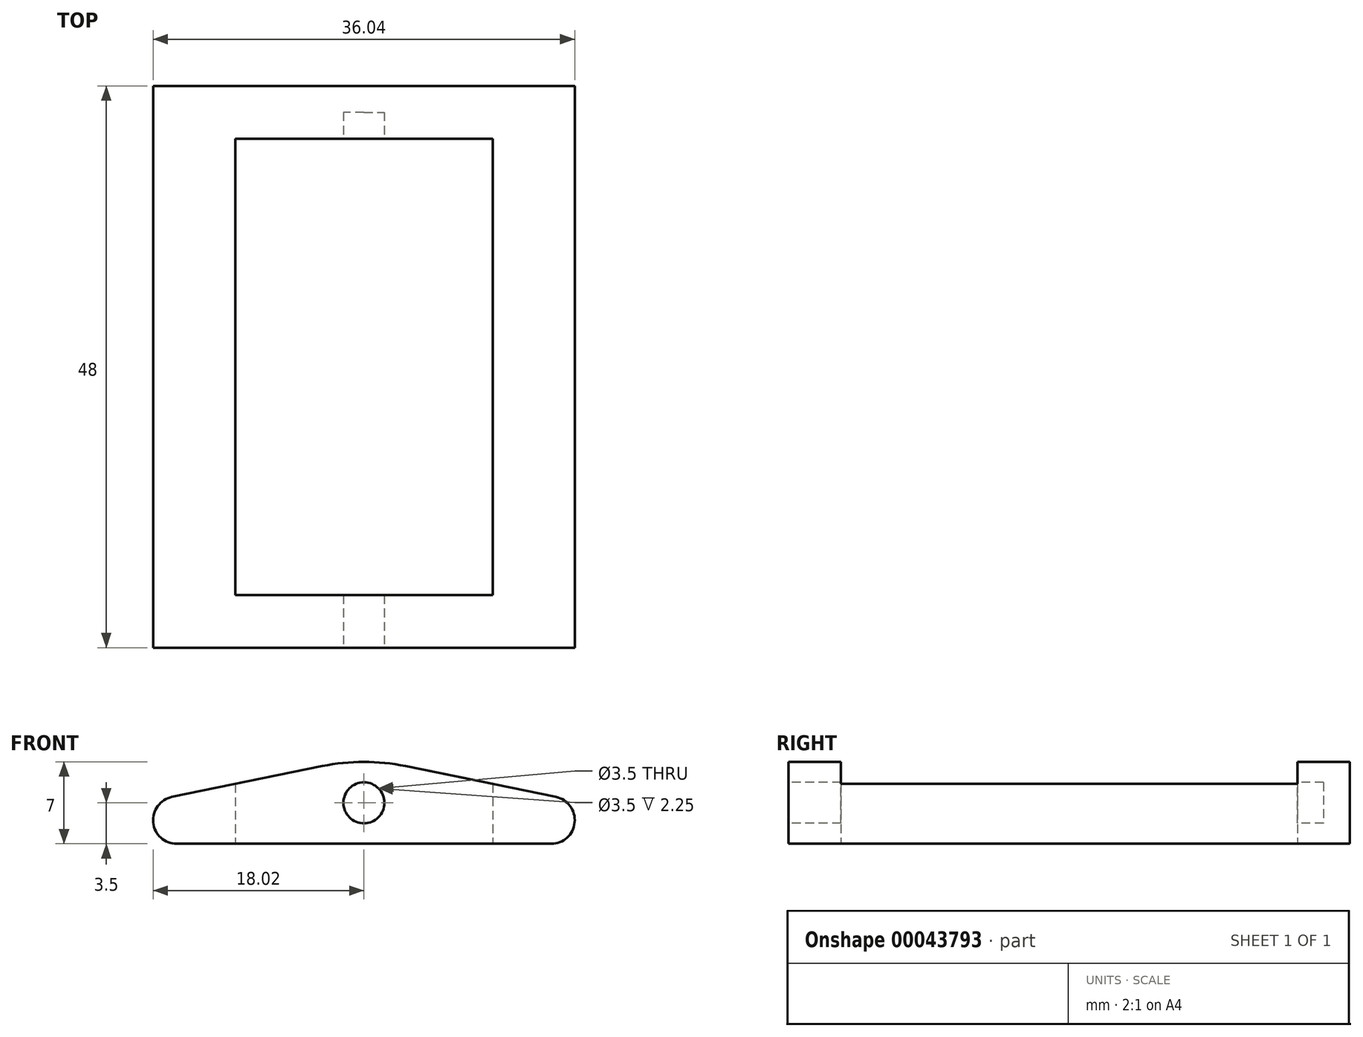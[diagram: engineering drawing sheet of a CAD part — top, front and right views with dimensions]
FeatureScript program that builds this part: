
annotation { "Feature Type Name" : "Feature", "Feature Type Description" : "" }
export const myFeature = defineFeature(function(context is Context, id is Id, definition is map)
    precondition{}
    {
        {
            var Q0;
            Q0=qCreatedBy(makeId("Front.planeOp"),FACE);
            var sketch = newSketch(context, id + "F0", { "sketchPlane" : qUnion([Q0])});
            skLineSegment(sketch, "E0", {"start": v(-16, 0) * mm, "end": v(16, 0) * mm});
            skArc(sketch, "E1", {"start": v(16, 0) * mm, "mid": v(18.01, 1.82) * mm, "end": v(16.4, 4) * mm});
            skArc(sketch, "E2", {"start": v(3.55, 6.64) * mm, "mid": v(0, 7) * mm, "end": v(-3.55, 6.64) * mm});
            skArc(sketch, "E3.MirrorCS", {"start": v(-16, 0) * mm, "mid": v(-18.01, 1.82) * mm, "end": v(-16.4, 4) * mm});
            skLineSegment(sketch, "E4", {"start": v(-16.4, 4) * mm, "end": v(-3.55, 6.64) * mm});
            skLineSegment(sketch, "E5", {"start": v(3.55, 6.64) * mm, "end": v(16.4, 4) * mm});
            skSolve(sketch);
        }
        {
            var Q0;
            Q0 = qSketchRegion(id + "F0", true);
            extrude(context, id + "F1", {"entities" : qUnion([Q0]), "endBound" : BoundingType.SYMMETRIC, "depth" : 48 * mm, "offsetDistance" : 25 * mm});
        }
        {
            var Q0;
            Q0=makeQuery(id+"F1.opExtrude","SWEPT_FACE",FACE,{"disambiguationData":[OSD([sQuery(id+"F0.wireOp",EDGE,"E0")])]});
            var sketch = newSketch(context, id + "F2", { "sketchPlane" : qUnion([Q0])});
            skLineSegment(sketch, "E6.bottom", {"start": v(-11, -19.5) * mm, "end": v(-4, -19.5) * mm});
            skLineSegment(sketch, "E6.top", {"start": v(-11, 19.5) * mm, "end": v(-4, 19.5) * mm});
            skLineSegment(sketch, "E6.left", {"start": v(-11, -19.5) * mm, "end": v(-11, 19.5) * mm});
            skLineSegment(sketch, "E6.right", {"start": v(-4, -19.5) * mm, "end": v(-4, 19.5) * mm, "construction": true});
            skPoint(sketch, "E6.middle", {"position": v(-7.5, 0) * mm});
            skLineSegment(sketch, "E7.MirrorCS", {"start": v(11, 19.5) * mm, "end": v(4, 19.5) * mm});
            skLineSegment(sketch, "E8.MirrorCS", {"start": v(11, -19.5) * mm, "end": v(11, 19.5) * mm});
            skLineSegment(sketch, "E9.MirrorCS", {"start": v(11, -19.5) * mm, "end": v(4, -19.5) * mm});
            skLineSegment(sketch, "E10.MirrorCS", {"start": v(4, -19.5) * mm, "end": v(4, 19.5) * mm, "construction": true});
            skLineSegment(sketch, "E11", {"start": v(-4, 19.5) * mm, "end": v(4, 19.5) * mm});
            skLineSegment(sketch, "E12", {"start": v(4, -19.5) * mm, "end": v(-4, -19.5) * mm});
            skLineSegment(sketch, "E13", {"start": v(4, -19.5) * mm, "end": v(4, -24) * mm});
            skPoint(sketch, "E14", {"position": v(4, -21.75) * mm});
            skSolve(sketch);
        }
        {
            var Q0;
            Q0=makeQuery(id+"F2.imprint","IMPRINT",FACE,{"disambiguationData":[TD([[makeQuery(id+"F2.imprint","IMPRINT",EDGE,{"derivedFrom":sQuery(id+"F2.wireOp",EDGE,"E6.bottom")}),1.0]])]});
            extrude(context, id + "F3", {"entities" : qUnion([Q0]), "operationType" : NewBodyOperationType.REMOVE, "endBound" : BoundingType.THROUGH_ALL, "oppositeDirection" : true, "depth" : 25 * mm, "offsetDistance" : 25 * mm});
        }
        {
            var Q0;
            Q0=makeQuery(id+"F1.opExtrude","CAP_FACE",FACE,{"disambiguationData":[OSD([sQuery(id+"F0.wireOp",EDGE,"E0"),sQuery(id+"F0.wireOp",EDGE,"E1"),sQuery(id+"F0.wireOp",EDGE,"E2"),sQuery(id+"F0.wireOp",EDGE,"E3.MirrorCS"),sQuery(id+"F0.wireOp",EDGE,"E4"),sQuery(id+"F0.wireOp",EDGE,"E5")])],"isStart":false});
            var sketch = newSketch(context, id + "F4", { "sketchPlane" : qUnion([Q0])});
            skCircle(sketch, "E15", {"center": v(0, 3.5) * mm, "radius": 1.75 * mm});
            skPoint(sketch, "E16", {"position": v(0, 5.25) * mm});
            skSolve(sketch);
        }
        {
            var Q0;
            Q0 = qSketchRegion(id + "F4", true);
            var Q1;
            Q1=sQuery(id+"F2.wireOp",VERTEX,"E14");
            extrude(context, id + "F5", {"entities" : qUnion([Q0]), "operationType" : NewBodyOperationType.REMOVE, "endBound" : BoundingType.UP_TO_VERTEX, "oppositeDirection" : true, "depth" : 25 * mm, "endBoundEntityVertex" : qUnion([Q1]), "offsetDistance" : 25 * mm});
        }
    });
